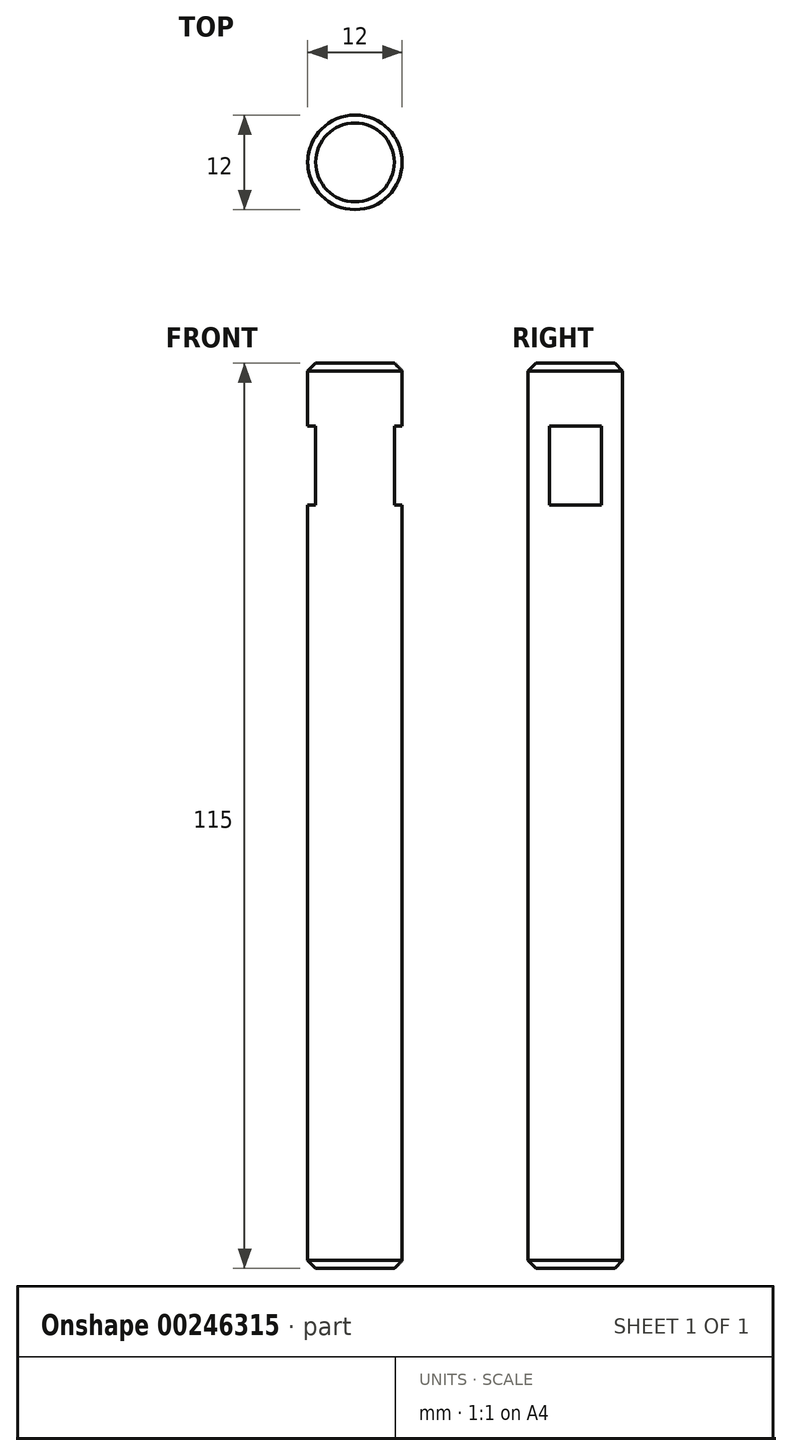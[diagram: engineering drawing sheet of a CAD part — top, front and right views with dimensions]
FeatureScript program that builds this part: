
annotation { "Feature Type Name" : "Feature", "Feature Type Description" : "" }
export const myFeature = defineFeature(function(context is Context, id is Id, definition is map)
    precondition{}
    {
        {
            var Q0;
            Q0=qCreatedBy(makeId("Top.planeOp"),FACE);
            var sketch = newSketch(context, id + "F0", { "sketchPlane" : qUnion([Q0])});
            skCircle(sketch, "E0", {"center": v(0, 0) * mm, "radius": 6 * mm});
            skSolve(sketch);
        }
        {
            var Q0;
            Q0 = qSketchRegion(id + "F0", true);
            extrude(context, id + "F1", {"entities" : qUnion([Q0]), "oppositeDirection" : true, "depth" : 115 * mm});
        }
        {
            var Q0;
            Q0=qCreatedBy(makeId("Front.planeOp"),FACE);
            var sketch = newSketch(context, id + "F2", { "sketchPlane" : qUnion([Q0])});
            skLineSegment(sketch, "E1", {"start": v(6, 0) * mm, "end": v(6, -115) * mm});
            skLineSegment(sketch, "E2", {"start": v(-6, -115) * mm, "end": v(-6, 0) * mm});
            skLineSegment(sketch, "E3", {"start": v(6, -8) * mm, "end": v(5, -8) * mm});
            skLineSegment(sketch, "E4", {"start": v(5, -8) * mm, "end": v(5, -18) * mm});
            skLineSegment(sketch, "E5", {"start": v(5, -18) * mm, "end": v(6, -18) * mm});
            skLineSegment(sketch, "E6", {"start": v(-6, -18) * mm, "end": v(-5, -18) * mm});
            skLineSegment(sketch, "E7", {"start": v(-5, -18) * mm, "end": v(-5, -8) * mm});
            skLineSegment(sketch, "E8", {"start": v(-5, -8) * mm, "end": v(-6, -8) * mm});
            skSolve(sketch);
        }
        {
            var Q0;
            Q0 = qSketchRegion(id + "F2", true);
            extrude(context, id + "F3", {"entities" : qUnion([Q0]), "operationType" : NewBodyOperationType.REMOVE, "endBound" : BoundingType.THROUGH_ALL, "oppositeDirection" : true, "depth" : 25 * mm, "hasSecondDirection" : true, "secondDirectionBound" : SecondDirectionBoundingType.THROUGH_ALL, "secondDirectionOppositeDirection" : false, "secondDirectionDepth" : 25 * mm});
        }
        {
            var Q0;
            Q0=makeQuery(id+"F1.opExtrude","CAP_EDGE",EDGE,{"disambiguationData":[OSD([sQuery(id+"F0.wireOp",EDGE,"E0")])],"isStart":true});
            var Q1;
            Q1=makeQuery(id+"F1.opExtrude","CAP_EDGE",EDGE,{"disambiguationData":[OSD([sQuery(id+"F0.wireOp",EDGE,"E0")])],"isStart":false});
            chamfer(context, id + "F4", {"entities" : qUnion([Q0, Q1]), "chamferType" : ChamferType.OFFSET_ANGLE, "width" : 1 * mm, "oppositeDirection" : false, "angle" : 45 * degree, "tangentPropagation" : true});
        }
    });
